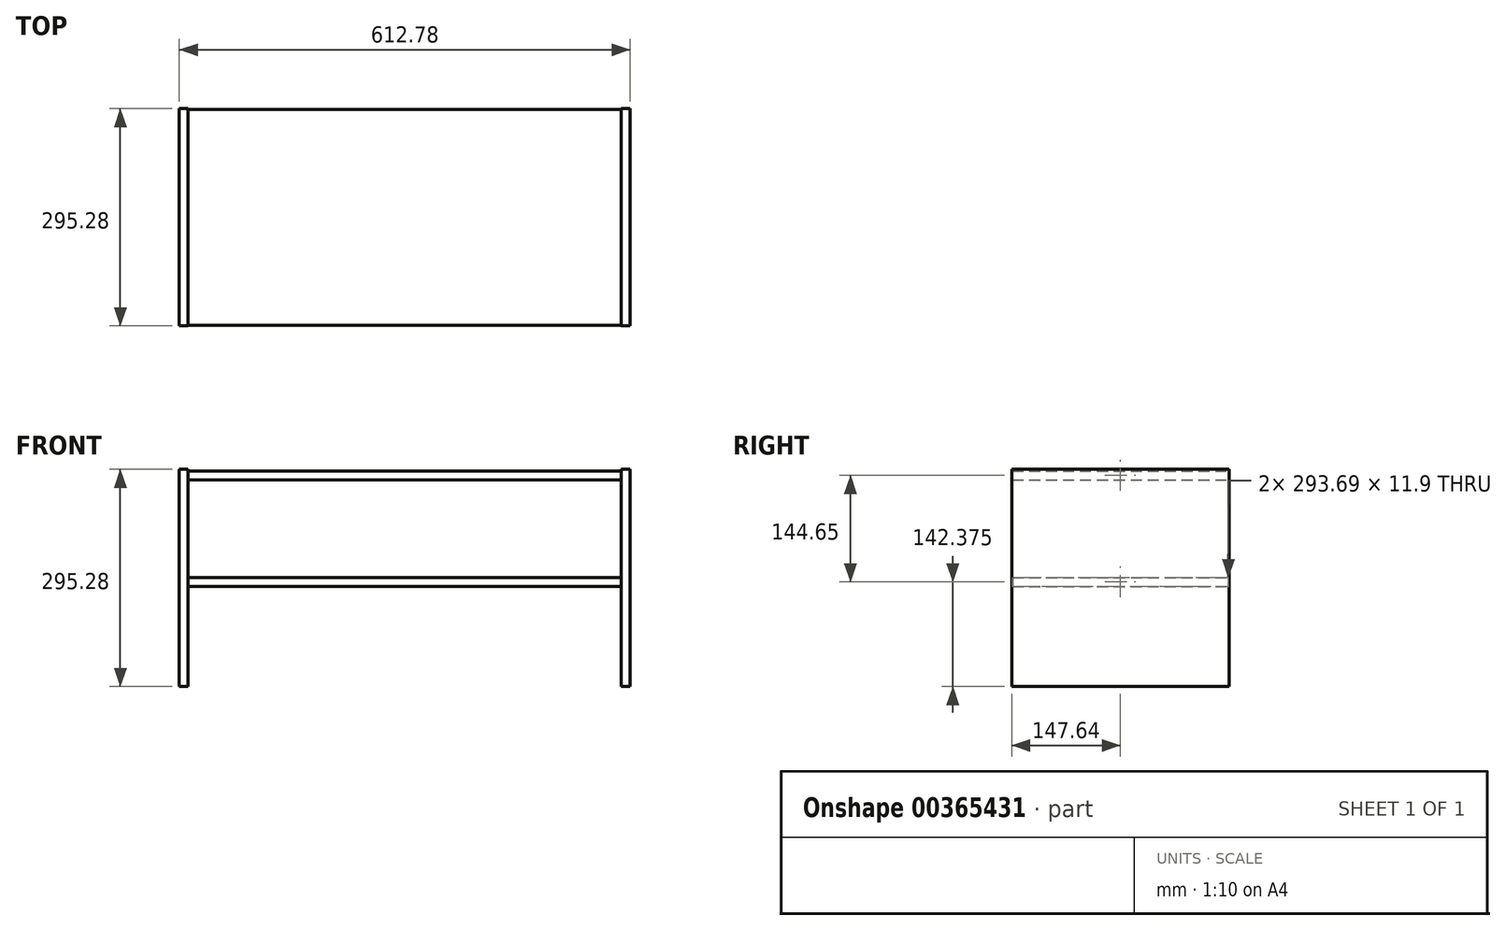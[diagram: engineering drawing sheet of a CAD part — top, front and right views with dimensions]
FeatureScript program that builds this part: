
annotation { "Feature Type Name" : "Feature", "Feature Type Description" : "" }
export const myFeature = defineFeature(function(context is Context, id is Id, definition is map)
    precondition{}
    {
        {
            var Q0;
            Q0=qCreatedBy(makeId("Front.planeOp"),FACE);
            var sketch = newSketch(context, id + "F0", { "sketchPlane" : qUnion([Q0])});
            skLineSegment(sketch, "E0", {"start": v(-306.39, 0) * mm, "end": v(306.39, 0) * mm, "construction": true});
            skLineSegment(sketch, "E1", {"start": v(-306.39, 0) * mm, "end": v(-306.39, 295.28) * mm});
            skLineSegment(sketch, "E2", {"start": v(-306.39, 295.28) * mm, "end": v(-294.29, 295.28) * mm});
            skLineSegment(sketch, "E3", {"start": v(-294.29, 295.28) * mm, "end": v(-294.29, 0) * mm});
            skLineSegment(sketch, "E4", {"start": v(294.29, 0) * mm, "end": v(294.29, 295.28) * mm});
            skLineSegment(sketch, "E5", {"start": v(294.29, 295.28) * mm, "end": v(306.39, 295.28) * mm});
            skLineSegment(sketch, "E6", {"start": v(306.39, 295.28) * mm, "end": v(306.39, 0) * mm});
            skLineSegment(sketch, "E7", {"start": v(-306.39, 0) * mm, "end": v(-294.29, 0) * mm});
            skLineSegment(sketch, "E8", {"start": v(294.29, 0) * mm, "end": v(306.39, 0) * mm});
            skLineSegment(sketch, "E9", {"start": v(-294.29, 292.98) * mm, "end": v(294.29, 292.98) * mm});
            skLineSegment(sketch, "E10", {"start": v(294.29, 281.08) * mm, "end": v(-294.29, 281.08) * mm});
            skLineSegment(sketch, "E11", {"start": v(-294.29, 148.33) * mm, "end": v(294.29, 148.33) * mm});
            skLineSegment(sketch, "E12", {"start": v(-294.29, 136.43) * mm, "end": v(294.29, 136.43) * mm});
            skSolve(sketch);
        }
        {
            var Q0;
            Q0=makeQuery(id+"F0.imprint","IMPRINT",FACE,{"disambiguationData":[TD([[makeQuery(id+"F0.imprint","IMPRINT",EDGE,{"derivedFrom":sQuery(id+"F0.wireOp",EDGE,"E1")}),-1.0]])]});
            var Q1;
            {var subQ6=sQuery(id+"F0.wireOp",EDGE,"E5");Q1=makeQuery(id+"F0.imprint","IMPRINT",FACE,{"disambiguationData":[TD([[makeQuery(id+"F0.imprint","IMPRINT",EDGE,{"derivedFrom":subQ6}),-1.0]])]});}
            extrude(context, id + "F1", {"entities" : qUnion([Q0, Q1]), "endBound" : BoundingType.SYMMETRIC, "depth" : 295.27 * mm});
        }
        {
            var Q0;
            {var subQ0=sQuery(id+"F0.wireOp",EDGE,"E9");Q0=makeQuery(id+"F0.imprint","IMPRINT",FACE,{"disambiguationData":[TD([[makeQuery(id+"F0.imprint","IMPRINT",EDGE,{"derivedFrom":subQ0}),-1.0]])]});}
            var Q1;
            {var subQ0=sQuery(id+"F0.wireOp",EDGE,"E11");Q1=makeQuery(id+"F0.imprint","IMPRINT",FACE,{"disambiguationData":[TD([[makeQuery(id+"F0.imprint","IMPRINT",EDGE,{"derivedFrom":subQ0}),-1.0]])]});}
            extrude(context, id + "F2", {"entities" : qUnion([Q0, Q1]), "operationType" : NewBodyOperationType.ADD, "endBound" : BoundingType.SYMMETRIC, "depth" : 293.7 * mm});
        }
    });
